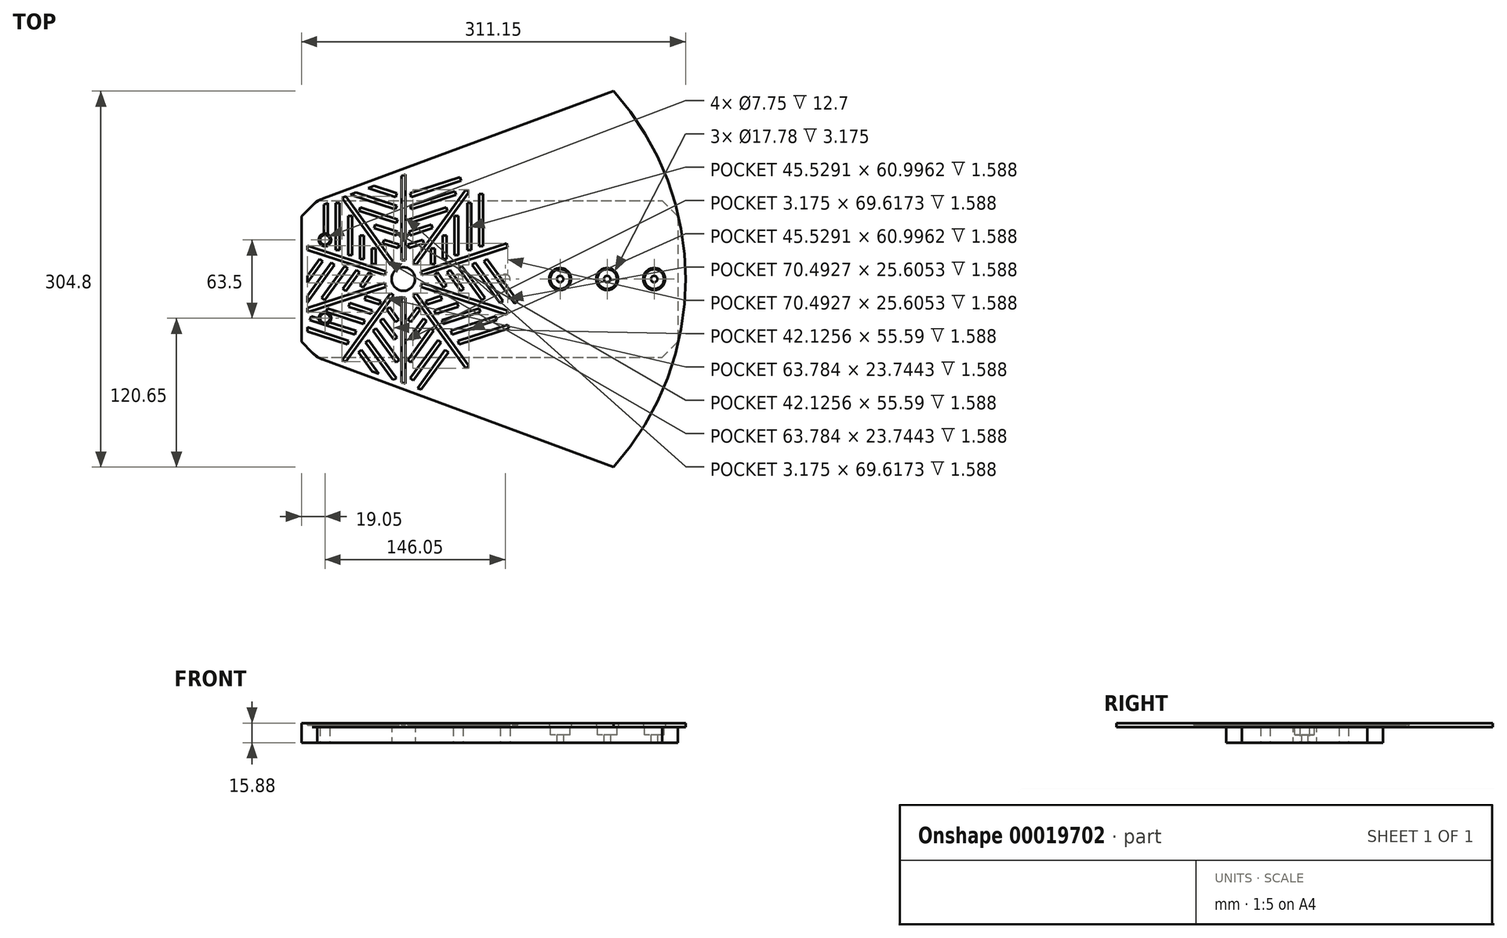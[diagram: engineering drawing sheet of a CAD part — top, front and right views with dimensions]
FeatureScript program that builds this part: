
annotation { "Feature Type Name" : "Feature", "Feature Type Description" : "" }
export const myFeature = defineFeature(function(context is Context, id is Id, definition is map)
    precondition{}
    {
        {
            var Q0;
            Q0=qCreatedBy(makeId("Top.planeOp"),FACE);
            var sketch = newSketch(context, id + "F0", { "sketchPlane" : qUnion([Q0])});
            skLineSegment(sketch, "E0.bottom", {"start": v(-127, 63.5) * mm, "end": v(177.8, 63.5) * mm});
            skLineSegment(sketch, "E0.top", {"start": v(-127, -63.5) * mm, "end": v(177.8, -63.5) * mm});
            skLineSegment(sketch, "E0.left", {"start": v(-127, 63.5) * mm, "end": v(-127, -63.5) * mm});
            skLineSegment(sketch, "E0.right", {"start": v(177.8, 63.5) * mm, "end": v(177.8, -63.5) * mm});
            skLineSegment(sketch, "E1", {"start": v(-127, 0) * mm, "end": v(177.8, 0) * mm, "construction": true});
            skSolve(sketch);
        }
        {
            var Q0;
            Q0 = qSketchRegion(id + "F0", true);
            extrude(context, id + "F1", {"entities" : qUnion([Q0]), "depth" : 12.7 * mm});
        }
        {
            var Q0;
            Q0=makeQuery(id+"F1.opExtrude","SWEPT_EDGE",EDGE,{"disambiguationData":[OSD([sQuery(id+"F0.wireOp",EDGE,"E0.top"),sQuery(id+"F0.wireOp",EDGE,"E0.left")])]});
            var Q1;
            Q1=makeQuery(id+"F1.opExtrude","SWEPT_EDGE",EDGE,{"disambiguationData":[OSD([sQuery(id+"F0.wireOp",EDGE,"E0.top"),sQuery(id+"F0.wireOp",EDGE,"E0.right")])]});
            var Q2;
            Q2=makeQuery(id+"F1.opExtrude","SWEPT_EDGE",EDGE,{"disambiguationData":[OSD([sQuery(id+"F0.wireOp",EDGE,"E0.bottom"),sQuery(id+"F0.wireOp",EDGE,"E0.right")])]});
            var Q3;
            Q3=makeQuery(id+"F1.opExtrude","SWEPT_EDGE",EDGE,{"disambiguationData":[OSD([sQuery(id+"F0.wireOp",EDGE,"E0.bottom"),sQuery(id+"F0.wireOp",EDGE,"E0.left")])]});
            chamfer(context, id + "F2", {"entities" : qUnion([Q0, Q1, Q2, Q3]), "width" : 12.7 * mm, "tangentPropagation" : true});
        }
        {
            var Q0;
            Q0=qCreatedBy(makeId("Top.planeOp"),FACE);
            var sketch = newSketch(context, id + "F3", { "sketchPlane" : qUnion([Q0])});
            skCircle(sketch, "E2", {"center": v(-44.45, 0) * mm, "radius": 9.53 * mm});
            skSolve(sketch);
        }
        {
            var Q0;
            Q0 = qSketchRegion(id + "F3", true);
            extrude(context, id + "F4", {"entities" : qUnion([Q0]), "operationType" : NewBodyOperationType.REMOVE, "depth" : 25.4 * mm});
        }
        {
            var Q0;
            Q0=qCreatedBy(makeId("Top.planeOp"),FACE);
            var sketch = newSketch(context, id + "F5", { "sketchPlane" : qUnion([Q0])});
            skCircle(sketch, "E3", {"center": v(0, 0) * mm, "radius": 3.87 * mm});
            skCircle(sketch, "E4", {"center": v(38.1, 0) * mm, "radius": 3.87 * mm});
            skSolve(sketch);
        }
        {
            var Q0;
            Q0 = qSketchRegion(id + "F5", true);
            extrude(context, id + "F6", {"entities" : qUnion([Q0]), "operationType" : NewBodyOperationType.REMOVE, "endBound" : BoundingType.THROUGH_ALL, "depth" : 25.4 * mm});
        }
        {
            var Q0;
            Q0=qCreatedBy(makeId("Top.planeOp"),FACE);
            var sketch = newSketch(context, id + "F7", { "sketchPlane" : qUnion([Q0])});
            skCircle(sketch, "E5", {"center": v(-107.95, 31.75) * mm, "radius": 3.87 * mm});
            skCircle(sketch, "E6", {"center": v(-107.95, -31.75) * mm, "radius": 3.87 * mm});
            skLineSegment(sketch, "E7", {"start": v(-107.95, 31.75) * mm, "end": v(-107.95, 0) * mm, "construction": true});
            skLineSegment(sketch, "E8", {"start": v(-107.95, 0) * mm, "end": v(-107.95, -31.75) * mm, "construction": true});
            skSolve(sketch);
        }
        {
            var Q0;
            Q0 = qSketchRegion(id + "F7", true);
            extrude(context, id + "F8", {"entities" : qUnion([Q0]), "operationType" : NewBodyOperationType.REMOVE, "endBound" : BoundingType.THROUGH_ALL, "depth" : 25.4 * mm});
        }
        {
            var Q0;
            Q0=qCreatedBy(makeId("Top.planeOp"),FACE);
            var sketch = newSketch(context, id + "F9", { "sketchPlane" : qUnion([Q0])});
            skCircle(sketch, "E9", {"center": v(82.55, 0) * mm, "radius": 2.6 * mm});
            skCircle(sketch, "E10", {"center": v(120.65, 0) * mm, "radius": 2.6 * mm});
            skCircle(sketch, "E11", {"center": v(158.75, 0) * mm, "radius": 2.6 * mm});
            skSolve(sketch);
        }
        {
            var Q0;
            Q0 = qSketchRegion(id + "F9", true);
            extrude(context, id + "F10", {"entities" : qUnion([Q0]), "operationType" : NewBodyOperationType.REMOVE, "endBound" : BoundingType.THROUGH_ALL, "depth" : 25.4 * mm});
        }
        {
            var Q0;
            Q0=makeQuery(id+"F1.opExtrude","CAP_FACE",FACE,{"disambiguationData":[OSD([sQuery(id+"F0.wireOp",EDGE,"E0.bottom"),sQuery(id+"F0.wireOp",EDGE,"E0.top"),sQuery(id+"F0.wireOp",EDGE,"E0.left"),sQuery(id+"F0.wireOp",EDGE,"E0.right")])],"isStart":false});
            var sketch = newSketch(context, id + "F11", { "sketchPlane" : qUnion([Q0])});
            skCircle(sketch, "E12", {"center": v(82.55, 0) * mm, "radius": 7.94 * mm});
            skCircle(sketch, "E13", {"center": v(120.65, 0) * mm, "radius": 7.94 * mm});
            skCircle(sketch, "E14", {"center": v(158.75, 0) * mm, "radius": 7.94 * mm});
            skSolve(sketch);
        }
        {
            var Q0;
            Q0 = qSketchRegion(id + "F11", true);
            extrude(context, id + "F12", {"entities" : qUnion([Q0]), "operationType" : NewBodyOperationType.REMOVE, "oppositeDirection" : true, "depth" : 6.35 * mm});
        }
        {
            var Q0;
            Q0=makeQuery(id+"F1.opExtrude","CAP_FACE",FACE,{"disambiguationData":[OSD([sQuery(id+"F0.wireOp",EDGE,"E0.bottom"),sQuery(id+"F0.wireOp",EDGE,"E0.top"),sQuery(id+"F0.wireOp",EDGE,"E0.left"),sQuery(id+"F0.wireOp",EDGE,"E0.right")])],"isStart":false});
            var sketch = newSketch(context, id + "F13", { "sketchPlane" : qUnion([Q0])});
            skLineSegment(sketch, "E15", {"start": v(-114.3, 63.5) * mm, "end": v(-127, 50.8) * mm});
            skLineSegment(sketch, "E16", {"start": v(-127, 50.8) * mm, "end": v(-127, -50.8) * mm});
            skLineSegment(sketch, "E17", {"start": v(-127, -50.8) * mm, "end": v(-114.3, -63.5) * mm});
            skCircle(sketch, "E18", {"center": v(-44.45, 0) * mm, "radius": 9.53 * mm});
            skCircle(sketch, "E19", {"center": v(-107.95, 31.75) * mm, "radius": 5.08 * mm});
            skCircle(sketch, "E20", {"center": v(-107.95, -31.75) * mm, "radius": 5.08 * mm});
            skCircle(sketch, "E21", {"center": v(82.55, 0) * mm, "radius": 8.9 * mm});
            skCircle(sketch, "E22", {"center": v(120.65, 0) * mm, "radius": 8.9 * mm});
            skCircle(sketch, "E23", {"center": v(158.75, 0) * mm, "radius": 8.9 * mm});
            skArc(sketch, "E24", {"start": v(125.94, -152.4) * mm, "mid": v(184.15, 0) * mm, "end": v(125.94, 152.4) * mm});
            skLineSegment(sketch, "E25", {"start": v(125.94, 152.4) * mm, "end": v(-114.3, 63.5) * mm});
            skLineSegment(sketch, "E26", {"start": v(125.94, -152.4) * mm, "end": v(-114.3, -63.5) * mm});
            skSolve(sketch);
        }
        {
            var Q0;
            Q0 = qSketchRegion(id + "F13", true);
            extrude(context, id + "F14", {"entities" : qUnion([Q0]), "depth" : 3.17 * mm});
        }
        {
            var Q0;
            Q0=makeQuery(id+"F14.opExtrude","SWEPT_EDGE",EDGE,{"disambiguationData":[OSD([sQuery(id+"F0.wireOp",EDGE,"E0.top"),sQuery(id+"F13.wireOp",EDGE,"57cfe194-b62b-4812-afb6-fe91522246ce"),sQuery(id+"F13.wireOp",EDGE,"734bb57e-c6ad-416e-8475-7722df8ed6a9.trimOffspring")])]});
            var Q1;
            Q1=makeQuery(id+"F14.opExtrude","SWEPT_EDGE",EDGE,{"disambiguationData":[OSD([sQuery(id+"F0.wireOp",EDGE,"E0.bottom"),sQuery(id+"F13.wireOp",EDGE,"7a98ed83-fb18-41a4-aa8c-db8b72770291"),sQuery(id+"F13.wireOp",EDGE,"12061aba-ef82-4446-8aa9-4ede10bfcb81")])]});
            fillet(context, id + "F15", {"entities" : qUnion([Q0, Q1]), "radius" : 25.4 * mm, "tangentPropagation" : true, "allowEdgeOverflow" : false});
        }
        {
            var Q0;
            Q0=makeQuery(id+"F14.opExtrude","CAP_FACE",FACE,{"disambiguationData":[OSD([sQuery(id+"F13.wireOp",EDGE,"E15"),sQuery(id+"F13.wireOp",EDGE,"E16"),sQuery(id+"F13.wireOp",EDGE,"E17"),sQuery(id+"F13.wireOp",EDGE,"E18"),sQuery(id+"F13.wireOp",EDGE,"E19"),sQuery(id+"F13.wireOp",EDGE,"E20"),sQuery(id+"F13.wireOp",EDGE,"E21"),sQuery(id+"F13.wireOp",EDGE,"E22"),sQuery(id+"F13.wireOp",EDGE,"E23"),sQuery(id+"F13.wireOp",EDGE,"E24"),sQuery(id+"F13.wireOp",EDGE,"E25"),sQuery(id+"F13.wireOp",EDGE,"E26")])],"isStart":false});
            var sketch = newSketch(context, id + "F16", { "sketchPlane" : qUnion([Q0])});
            skLineSegment(sketch, "E27.bottom", {"start": v(-46.04, 15.24) * mm, "end": v(-42.86, 15.24) * mm});
            skLineSegment(sketch, "E27.top", {"start": v(-46.04, 88.33) * mm, "end": v(-42.86, 88.33) * mm});
            skLineSegment(sketch, "E27.left", {"start": v(-46.04, 15.24) * mm, "end": v(-46.04, 88.33) * mm});
            skLineSegment(sketch, "E27.right", {"start": v(-42.86, 15.24) * mm, "end": v(-42.86, 88.33) * mm});
            skLineSegment(sketch, "E28.1.0", {"start": v(-54.7, 11.4) * mm, "end": v(-97.65, 70.53) * mm});
            skLineSegment(sketch, "E28.1.1", {"start": v(-52.12, 13.26) * mm, "end": v(-95.08, 72.4) * mm});
            skLineSegment(sketch, "E28.1.2", {"start": v(-97.65, 70.53) * mm, "end": v(-95.08, 72.4) * mm});
            skLineSegment(sketch, "E28.1.3", {"start": v(-54.7, 11.4) * mm, "end": v(-52.12, 13.26) * mm});
            skLineSegment(sketch, "E28.2.0", {"start": v(-59.43, 3.2) * mm, "end": v(-128.95, 25.79) * mm});
            skLineSegment(sketch, "E28.2.1", {"start": v(-58.45, 6.22) * mm, "end": v(-127.97, 28.8) * mm});
            skLineSegment(sketch, "E28.2.2", {"start": v(-128.95, 25.79) * mm, "end": v(-127.97, 28.8) * mm});
            skLineSegment(sketch, "E28.2.3", {"start": v(-59.43, 3.2) * mm, "end": v(-58.45, 6.22) * mm});
            skLineSegment(sketch, "E28.3.0", {"start": v(-58.45, -6.22) * mm, "end": v(-127.97, -28.8) * mm});
            skLineSegment(sketch, "E28.3.1", {"start": v(-59.43, -3.2) * mm, "end": v(-128.95, -25.79) * mm});
            skLineSegment(sketch, "E28.3.2", {"start": v(-127.97, -28.8) * mm, "end": v(-128.95, -25.79) * mm});
            skLineSegment(sketch, "E28.3.3", {"start": v(-58.45, -6.22) * mm, "end": v(-59.43, -3.2) * mm});
            skLineSegment(sketch, "E28.4.0", {"start": v(-52.12, -13.26) * mm, "end": v(-95.08, -72.4) * mm});
            skLineSegment(sketch, "E28.4.1", {"start": v(-54.7, -11.4) * mm, "end": v(-97.65, -70.53) * mm});
            skLineSegment(sketch, "E28.4.2", {"start": v(-95.08, -72.4) * mm, "end": v(-97.65, -70.53) * mm});
            skLineSegment(sketch, "E28.4.3", {"start": v(-52.12, -13.26) * mm, "end": v(-54.7, -11.4) * mm});
            skLineSegment(sketch, "E28.5.0", {"start": v(-42.86, -15.24) * mm, "end": v(-42.86, -88.33) * mm});
            skLineSegment(sketch, "E28.5.1", {"start": v(-46.04, -15.24) * mm, "end": v(-46.04, -88.33) * mm});
            skLineSegment(sketch, "E28.5.2", {"start": v(-42.86, -88.33) * mm, "end": v(-46.04, -88.33) * mm});
            skLineSegment(sketch, "E28.5.3", {"start": v(-42.86, -15.24) * mm, "end": v(-46.04, -15.24) * mm});
            skLineSegment(sketch, "E28.6.0", {"start": v(-34.2, -11.4) * mm, "end": v(8.75, -70.53) * mm});
            skLineSegment(sketch, "E28.6.1", {"start": v(-36.78, -13.26) * mm, "end": v(6.18, -72.4) * mm});
            skLineSegment(sketch, "E28.6.2", {"start": v(8.75, -70.53) * mm, "end": v(6.18, -72.4) * mm});
            skLineSegment(sketch, "E28.6.3", {"start": v(-34.2, -11.4) * mm, "end": v(-36.78, -13.26) * mm});
            skLineSegment(sketch, "E28.7.0", {"start": v(-29.47, -3.2) * mm, "end": v(40.05, -25.79) * mm});
            skLineSegment(sketch, "E28.7.1", {"start": v(-30.45, -6.22) * mm, "end": v(39.07, -28.8) * mm});
            skLineSegment(sketch, "E28.7.2", {"start": v(40.05, -25.79) * mm, "end": v(39.07, -28.8) * mm});
            skLineSegment(sketch, "E28.7.3", {"start": v(-29.47, -3.2) * mm, "end": v(-30.45, -6.22) * mm});
            skLineSegment(sketch, "E28.8.0", {"start": v(-30.45, 6.22) * mm, "end": v(39.07, 28.8) * mm});
            skLineSegment(sketch, "E28.8.1", {"start": v(-29.47, 3.2) * mm, "end": v(40.05, 25.79) * mm});
            skLineSegment(sketch, "E28.8.2", {"start": v(39.07, 28.8) * mm, "end": v(40.05, 25.79) * mm});
            skLineSegment(sketch, "E28.8.3", {"start": v(-30.45, 6.22) * mm, "end": v(-29.47, 3.2) * mm});
            skLineSegment(sketch, "E28.9.0", {"start": v(-36.78, 13.26) * mm, "end": v(6.18, 72.4) * mm});
            skLineSegment(sketch, "E28.9.1", {"start": v(-34.2, 11.4) * mm, "end": v(8.75, 70.53) * mm});
            skLineSegment(sketch, "E28.9.2", {"start": v(6.18, 72.4) * mm, "end": v(8.75, 70.53) * mm});
            skLineSegment(sketch, "E28.9.3", {"start": v(-36.78, 13.26) * mm, "end": v(-34.2, 11.4) * mm});
            skPoint(sketch, "E28.center", {"position": v(-44.45, 0) * mm});
            skLineSegment(sketch, "E29.bottom", {"start": v(0.17, 51.12) * mm, "end": v(-3, 51.12) * mm});
            skLineSegment(sketch, "E29.top", {"start": v(0.17, 19.37) * mm, "end": v(-3, 19.37) * mm});
            skLineSegment(sketch, "E29.left", {"start": v(0.17, 51.12) * mm, "end": v(0.17, 19.37) * mm});
            skLineSegment(sketch, "E29.right", {"start": v(-3, 51.12) * mm, "end": v(-3, 19.37) * mm});
            skLineSegment(sketch, "E30.bottom", {"start": v(-12.53, 35.33) * mm, "end": v(-9.35, 35.33) * mm});
            skLineSegment(sketch, "E30.top", {"start": v(-12.53, 16.28) * mm, "end": v(-9.35, 16.28) * mm});
            skLineSegment(sketch, "E30.left", {"start": v(-12.53, 35.33) * mm, "end": v(-12.53, 16.28) * mm});
            skLineSegment(sketch, "E30.right", {"start": v(-9.35, 35.33) * mm, "end": v(-9.35, 16.28) * mm});
            skLineSegment(sketch, "E31.bottom", {"start": v(7.3, 61.65) * mm, "end": v(10.48, 61.65) * mm});
            skLineSegment(sketch, "E31.top", {"start": v(7.3, 23.55) * mm, "end": v(10.48, 23.55) * mm});
            skLineSegment(sketch, "E31.left", {"start": v(7.3, 61.65) * mm, "end": v(7.3, 23.55) * mm});
            skLineSegment(sketch, "E31.right", {"start": v(10.48, 61.65) * mm, "end": v(10.48, 23.55) * mm});
            skLineSegment(sketch, "E32.bottom", {"start": v(-22.05, 24.68) * mm, "end": v(-18.88, 24.68) * mm});
            skLineSegment(sketch, "E32.top", {"start": v(-22.05, 11.98) * mm, "end": v(-18.88, 11.98) * mm});
            skLineSegment(sketch, "E32.left", {"start": v(-22.05, 24.68) * mm, "end": v(-22.05, 11.98) * mm});
            skLineSegment(sketch, "E32.right", {"start": v(-18.88, 24.68) * mm, "end": v(-18.88, 11.98) * mm});
            skLineSegment(sketch, "E33.bottom", {"start": v(16.83, 26.62) * mm, "end": v(20, 26.62) * mm});
            skLineSegment(sketch, "E33.top", {"start": v(16.83, 68.97) * mm, "end": v(20, 68.97) * mm});
            skLineSegment(sketch, "E33.left", {"start": v(16.83, 26.62) * mm, "end": v(16.83, 68.97) * mm});
            skLineSegment(sketch, "E33.right", {"start": v(20, 26.62) * mm, "end": v(20, 68.97) * mm});
            skLineSegment(sketch, "E34", {"start": v(-29.96, 4.7) * mm, "end": v(39.56, 27.3) * mm, "construction": true});
            skLineSegment(sketch, "E35.MirrorCS", {"start": v(23.34, 16.35) * mm, "end": v(48.24, -17.91) * mm});
            skLineSegment(sketch, "E36.MirrorCS", {"start": v(20.77, 14.49) * mm, "end": v(45.67, -19.78) * mm});
            skLineSegment(sketch, "E37.MirrorCS", {"start": v(45.67, -19.78) * mm, "end": v(48.24, -17.91) * mm});
            skLineSegment(sketch, "E38.MirrorCS", {"start": v(20.77, 14.49) * mm, "end": v(23.34, 16.35) * mm});
            skLineSegment(sketch, "E39.MirrorCS", {"start": v(36.23, -17.59) * mm, "end": v(13.83, 13.24) * mm});
            skLineSegment(sketch, "E40.MirrorCS", {"start": v(33.66, -19.45) * mm, "end": v(11.26, 11.37) * mm});
            skLineSegment(sketch, "E41.MirrorCS", {"start": v(33.66, -19.45) * mm, "end": v(36.23, -17.59) * mm});
            skLineSegment(sketch, "E42.MirrorCS", {"start": v(11.26, 11.37) * mm, "end": v(13.83, 13.24) * mm});
            skLineSegment(sketch, "E43.MirrorCS", {"start": v(21.7, -15.13) * mm, "end": v(19.13, -17) * mm});
            skLineSegment(sketch, "E44.MirrorCS", {"start": v(21.7, -15.13) * mm, "end": v(3.04, 10.56) * mm});
            skLineSegment(sketch, "E45.MirrorCS", {"start": v(19.13, -17) * mm, "end": v(0.47, 8.69) * mm});
            skLineSegment(sketch, "E46.MirrorCS", {"start": v(3.04, 10.56) * mm, "end": v(0.47, 8.69) * mm});
            skLineSegment(sketch, "E47.MirrorCS", {"start": v(4.7, -7.95) * mm, "end": v(-6.49, 7.46) * mm});
            skLineSegment(sketch, "E48.MirrorCS", {"start": v(2.14, -9.82) * mm, "end": v(-9.06, 5.6) * mm});
            skLineSegment(sketch, "E49.MirrorCS", {"start": v(2.14, -9.82) * mm, "end": v(4.7, -7.95) * mm});
            skLineSegment(sketch, "E50.MirrorCS", {"start": v(-9.06, 5.6) * mm, "end": v(-6.49, 7.46) * mm});
            skLineSegment(sketch, "E51.MirrorCS", {"start": v(-11.82, -6.8) * mm, "end": v(-9.25, -4.94) * mm});
            skLineSegment(sketch, "E52.MirrorCS", {"start": v(-9.25, -4.94) * mm, "end": v(-16.72, 5.34) * mm});
            skLineSegment(sketch, "E53.MirrorCS", {"start": v(-19.29, 3.47) * mm, "end": v(-16.72, 5.34) * mm});
            skLineSegment(sketch, "E54.MirrorCS", {"start": v(-11.82, -6.8) * mm, "end": v(-19.29, 3.47) * mm});
            skLineSegment(sketch, "E55.1.0", {"start": v(-49.85, 69.53) * mm, "end": v(-90.13, 82.62) * mm});
            skLineSegment(sketch, "E55.1.1", {"start": v(-91.1, 79.6) * mm, "end": v(-90.13, 82.62) * mm});
            skLineSegment(sketch, "E55.1.2", {"start": v(-50.83, 66.5) * mm, "end": v(-49.85, 69.53) * mm});
            skLineSegment(sketch, "E55.1.3", {"start": v(-50.83, 66.5) * mm, "end": v(-91.1, 79.6) * mm});
            skLineSegment(sketch, "E55.1.4", {"start": v(-86.1, 71.3) * mm, "end": v(-49.87, 59.52) * mm});
            skLineSegment(sketch, "E55.1.5", {"start": v(-87.09, 68.27) * mm, "end": v(-50.85, 56.5) * mm});
            skLineSegment(sketch, "E55.1.6", {"start": v(-50.85, 56.5) * mm, "end": v(-49.87, 59.52) * mm});
            skLineSegment(sketch, "E55.1.7", {"start": v(-87.09, 68.27) * mm, "end": v(-86.1, 71.3) * mm});
            skLineSegment(sketch, "E55.1.8", {"start": v(-79.28, 58.24) * mm, "end": v(-80.26, 55.22) * mm});
            skLineSegment(sketch, "E55.1.9", {"start": v(-79.28, 58.24) * mm, "end": v(-49.09, 48.42) * mm});
            skLineSegment(sketch, "E55.1.10", {"start": v(-80.26, 55.22) * mm, "end": v(-50.07, 45.4) * mm});
            skLineSegment(sketch, "E55.1.11", {"start": v(-49.09, 48.42) * mm, "end": v(-50.07, 45.4) * mm});
            skLineSegment(sketch, "E55.1.12", {"start": v(-67.2, 44.3) * mm, "end": v(-49.09, 38.4) * mm});
            skLineSegment(sketch, "E55.1.13", {"start": v(-68.18, 41.28) * mm, "end": v(-50.07, 35.39) * mm});
            skLineSegment(sketch, "E55.1.14", {"start": v(-68.18, 41.28) * mm, "end": v(-67.2, 44.3) * mm});
            skLineSegment(sketch, "E55.1.15", {"start": v(-50.07, 35.39) * mm, "end": v(-49.09, 38.4) * mm});
            skLineSegment(sketch, "E55.1.16", {"start": v(-60.02, 31.95) * mm, "end": v(-47.94, 28.02) * mm});
            skLineSegment(sketch, "E55.1.17", {"start": v(-61, 28.93) * mm, "end": v(-60.02, 31.95) * mm});
            skLineSegment(sketch, "E55.1.18", {"start": v(-61, 28.93) * mm, "end": v(-48.92, 25) * mm});
            skLineSegment(sketch, "E55.1.19", {"start": v(-48.92, 25) * mm, "end": v(-47.94, 28.02) * mm});
            skLineSegment(sketch, "E55.1.20", {"start": v(-39.98, 25) * mm, "end": v(-40.96, 28.02) * mm});
            skLineSegment(sketch, "E55.1.21", {"start": v(-28.88, 31.95) * mm, "end": v(-40.96, 28.02) * mm});
            skLineSegment(sketch, "E55.1.22", {"start": v(-27.9, 28.93) * mm, "end": v(-39.98, 25) * mm});
            skLineSegment(sketch, "E55.1.23", {"start": v(-27.9, 28.93) * mm, "end": v(-28.88, 31.95) * mm});
            skLineSegment(sketch, "E55.1.24", {"start": v(-38.83, 35.39) * mm, "end": v(-39.81, 38.4) * mm});
            skLineSegment(sketch, "E55.1.25", {"start": v(-21.7, 44.3) * mm, "end": v(-39.81, 38.4) * mm});
            skLineSegment(sketch, "E55.1.26", {"start": v(-20.72, 41.28) * mm, "end": v(-38.83, 35.39) * mm});
            skLineSegment(sketch, "E55.1.27", {"start": v(-20.72, 41.28) * mm, "end": v(-21.7, 44.3) * mm});
            skLineSegment(sketch, "E55.1.28", {"start": v(-8.64, 55.22) * mm, "end": v(-38.83, 45.4) * mm});
            skLineSegment(sketch, "E55.1.29", {"start": v(-9.62, 58.24) * mm, "end": v(-39.81, 48.42) * mm});
            skLineSegment(sketch, "E55.1.30", {"start": v(-9.62, 58.24) * mm, "end": v(-8.64, 55.22) * mm});
            skLineSegment(sketch, "E55.1.31", {"start": v(-39.81, 48.42) * mm, "end": v(-38.83, 45.4) * mm});
            skLineSegment(sketch, "E55.1.32", {"start": v(-2.8, 71.3) * mm, "end": v(-39.03, 59.52) * mm});
            skLineSegment(sketch, "E55.1.33", {"start": v(-1.81, 68.27) * mm, "end": v(-38.05, 56.5) * mm});
            skLineSegment(sketch, "E55.1.34", {"start": v(-38.05, 56.5) * mm, "end": v(-39.03, 59.52) * mm});
            skLineSegment(sketch, "E55.1.35", {"start": v(-1.81, 68.27) * mm, "end": v(-2.8, 71.3) * mm});
            skLineSegment(sketch, "E55.1.36", {"start": v(-38.07, 66.5) * mm, "end": v(2.2, 79.6) * mm});
            skLineSegment(sketch, "E55.1.37", {"start": v(-39.05, 69.53) * mm, "end": v(1.23, 82.62) * mm});
            skLineSegment(sketch, "E55.1.38", {"start": v(2.2, 79.6) * mm, "end": v(1.23, 82.62) * mm});
            skLineSegment(sketch, "E55.1.39", {"start": v(-38.07, 66.5) * mm, "end": v(-39.05, 69.53) * mm});
            skLineSegment(sketch, "E55.2.0", {"start": v(-112.24, 16.35) * mm, "end": v(-137.14, -17.91) * mm});
            skLineSegment(sketch, "E55.2.1", {"start": v(-134.57, -19.78) * mm, "end": v(-137.14, -17.91) * mm});
            skLineSegment(sketch, "E55.2.2", {"start": v(-109.67, 14.49) * mm, "end": v(-112.24, 16.35) * mm});
            skLineSegment(sketch, "E55.2.3", {"start": v(-109.67, 14.49) * mm, "end": v(-134.57, -19.78) * mm});
            skLineSegment(sketch, "E55.2.4", {"start": v(-125.13, -17.59) * mm, "end": v(-102.73, 13.24) * mm});
            skLineSegment(sketch, "E55.2.5", {"start": v(-122.56, -19.45) * mm, "end": v(-100.16, 11.37) * mm});
            skLineSegment(sketch, "E55.2.6", {"start": v(-100.16, 11.37) * mm, "end": v(-102.73, 13.24) * mm});
            skLineSegment(sketch, "E55.2.7", {"start": v(-122.56, -19.45) * mm, "end": v(-125.13, -17.59) * mm});
            skLineSegment(sketch, "E55.2.8", {"start": v(-110.6, -15.13) * mm, "end": v(-108.03, -17) * mm});
            skLineSegment(sketch, "E55.2.9", {"start": v(-110.6, -15.13) * mm, "end": v(-91.94, 10.56) * mm});
            skLineSegment(sketch, "E55.2.10", {"start": v(-108.03, -17) * mm, "end": v(-89.37, 8.69) * mm});
            skLineSegment(sketch, "E55.2.11", {"start": v(-91.94, 10.56) * mm, "end": v(-89.37, 8.69) * mm});
            skLineSegment(sketch, "E55.2.12", {"start": v(-93.6, -7.95) * mm, "end": v(-82.41, 7.46) * mm});
            skLineSegment(sketch, "E55.2.13", {"start": v(-91.04, -9.82) * mm, "end": v(-79.84, 5.6) * mm});
            skLineSegment(sketch, "E55.2.14", {"start": v(-91.04, -9.82) * mm, "end": v(-93.6, -7.95) * mm});
            skLineSegment(sketch, "E55.2.15", {"start": v(-79.84, 5.6) * mm, "end": v(-82.41, 7.46) * mm});
            skLineSegment(sketch, "E55.2.16", {"start": v(-79.65, -4.94) * mm, "end": v(-72.18, 5.34) * mm});
            skLineSegment(sketch, "E55.2.17", {"start": v(-77.08, -6.8) * mm, "end": v(-79.65, -4.94) * mm});
            skLineSegment(sketch, "E55.2.18", {"start": v(-77.08, -6.8) * mm, "end": v(-69.61, 3.47) * mm});
            skLineSegment(sketch, "E55.2.19", {"start": v(-69.61, 3.47) * mm, "end": v(-72.18, 5.34) * mm});
            skLineSegment(sketch, "E55.2.20", {"start": v(-66.85, 11.98) * mm, "end": v(-70.02, 11.98) * mm});
            skLineSegment(sketch, "E55.2.21", {"start": v(-70.02, 24.68) * mm, "end": v(-70.02, 11.98) * mm});
            skLineSegment(sketch, "E55.2.22", {"start": v(-66.85, 24.68) * mm, "end": v(-66.85, 11.98) * mm});
            skLineSegment(sketch, "E55.2.23", {"start": v(-66.85, 24.68) * mm, "end": v(-70.02, 24.68) * mm});
            skLineSegment(sketch, "E55.2.24", {"start": v(-76.37, 16.28) * mm, "end": v(-79.55, 16.28) * mm});
            skLineSegment(sketch, "E55.2.25", {"start": v(-79.55, 35.33) * mm, "end": v(-79.55, 16.28) * mm});
            skLineSegment(sketch, "E55.2.26", {"start": v(-76.37, 35.33) * mm, "end": v(-76.37, 16.28) * mm});
            skLineSegment(sketch, "E55.2.27", {"start": v(-76.37, 35.33) * mm, "end": v(-79.55, 35.33) * mm});
            skLineSegment(sketch, "E55.2.28", {"start": v(-85.9, 51.12) * mm, "end": v(-85.9, 19.37) * mm});
            skLineSegment(sketch, "E55.2.29", {"start": v(-89.07, 51.12) * mm, "end": v(-89.07, 19.37) * mm});
            skLineSegment(sketch, "E55.2.30", {"start": v(-89.07, 51.12) * mm, "end": v(-85.9, 51.12) * mm});
            skLineSegment(sketch, "E55.2.31", {"start": v(-89.07, 19.37) * mm, "end": v(-85.9, 19.37) * mm});
            skLineSegment(sketch, "E55.2.32", {"start": v(-99.38, 61.65) * mm, "end": v(-99.38, 23.55) * mm});
            skLineSegment(sketch, "E55.2.33", {"start": v(-96.2, 61.65) * mm, "end": v(-96.2, 23.55) * mm});
            skLineSegment(sketch, "E55.2.34", {"start": v(-96.2, 23.55) * mm, "end": v(-99.38, 23.55) * mm});
            skLineSegment(sketch, "E55.2.35", {"start": v(-96.2, 61.65) * mm, "end": v(-99.38, 61.65) * mm});
            skLineSegment(sketch, "E55.2.36", {"start": v(-105.73, 26.62) * mm, "end": v(-105.73, 68.97) * mm});
            skLineSegment(sketch, "E55.2.37", {"start": v(-108.9, 26.62) * mm, "end": v(-108.9, 68.97) * mm});
            skLineSegment(sketch, "E55.2.38", {"start": v(-105.73, 68.97) * mm, "end": v(-108.9, 68.97) * mm});
            skLineSegment(sketch, "E55.2.39", {"start": v(-105.73, 26.62) * mm, "end": v(-108.9, 26.62) * mm});
            skLineSegment(sketch, "E55.3.0", {"start": v(-80.95, -59.42) * mm, "end": v(-56.06, -93.69) * mm});
            skLineSegment(sketch, "E55.3.1", {"start": v(-53.49, -91.82) * mm, "end": v(-56.06, -93.69) * mm});
            skLineSegment(sketch, "E55.3.2", {"start": v(-78.38, -57.56) * mm, "end": v(-80.95, -59.42) * mm});
            skLineSegment(sketch, "E55.3.3", {"start": v(-78.38, -57.56) * mm, "end": v(-53.49, -91.82) * mm});
            skLineSegment(sketch, "E55.3.4", {"start": v(-52.65, -82.16) * mm, "end": v(-75.05, -51.34) * mm});
            skLineSegment(sketch, "E55.3.5", {"start": v(-50.09, -80.3) * mm, "end": v(-72.48, -49.47) * mm});
            skLineSegment(sketch, "E55.3.6", {"start": v(-72.48, -49.47) * mm, "end": v(-75.05, -51.34) * mm});
            skLineSegment(sketch, "E55.3.7", {"start": v(-50.09, -80.3) * mm, "end": v(-52.65, -82.16) * mm});
            skLineSegment(sketch, "E55.3.8", {"start": v(-50.5, -67.59) * mm, "end": v(-47.93, -65.72) * mm});
            skLineSegment(sketch, "E55.3.9", {"start": v(-50.5, -67.59) * mm, "end": v(-69.16, -41.9) * mm});
            skLineSegment(sketch, "E55.3.10", {"start": v(-47.93, -65.72) * mm, "end": v(-66.6, -40.03) * mm});
            skLineSegment(sketch, "E55.3.11", {"start": v(-69.16, -41.9) * mm, "end": v(-66.6, -40.03) * mm});
            skLineSegment(sketch, "E55.3.12", {"start": v(-52.08, -49.21) * mm, "end": v(-63.28, -33.8) * mm});
            skLineSegment(sketch, "E55.3.13", {"start": v(-49.51, -47.34) * mm, "end": v(-60.7, -31.93) * mm});
            skLineSegment(sketch, "E55.3.14", {"start": v(-49.51, -47.34) * mm, "end": v(-52.08, -49.21) * mm});
            skLineSegment(sketch, "E55.3.15", {"start": v(-60.7, -31.93) * mm, "end": v(-63.28, -33.8) * mm});
            skLineSegment(sketch, "E55.3.16", {"start": v(-50.63, -35) * mm, "end": v(-58.1, -24.72) * mm});
            skLineSegment(sketch, "E55.3.17", {"start": v(-48.06, -33.13) * mm, "end": v(-50.63, -35) * mm});
            skLineSegment(sketch, "E55.3.18", {"start": v(-48.06, -33.13) * mm, "end": v(-55.53, -22.86) * mm});
            skLineSegment(sketch, "E55.3.19", {"start": v(-55.53, -22.86) * mm, "end": v(-58.1, -24.72) * mm});
            skLineSegment(sketch, "E55.3.20", {"start": v(-62.77, -17.6) * mm, "end": v(-63.75, -20.62) * mm});
            skLineSegment(sketch, "E55.3.21", {"start": v(-75.83, -16.7) * mm, "end": v(-63.75, -20.62) * mm});
            skLineSegment(sketch, "E55.3.22", {"start": v(-74.84, -13.67) * mm, "end": v(-62.77, -17.6) * mm});
            skLineSegment(sketch, "E55.3.23", {"start": v(-74.84, -13.67) * mm, "end": v(-75.83, -16.7) * mm});
            skLineSegment(sketch, "E55.3.24", {"start": v(-69.8, -25.33) * mm, "end": v(-70.78, -28.35) * mm});
            skLineSegment(sketch, "E55.3.25", {"start": v(-88.9, -22.46) * mm, "end": v(-70.78, -28.35) * mm});
            skLineSegment(sketch, "E55.3.26", {"start": v(-87.91, -19.44) * mm, "end": v(-69.8, -25.33) * mm});
            skLineSegment(sketch, "E55.3.27", {"start": v(-87.91, -19.44) * mm, "end": v(-88.9, -22.46) * mm});
            skLineSegment(sketch, "E55.3.28", {"start": v(-105.88, -23.62) * mm, "end": v(-75.68, -33.43) * mm});
            skLineSegment(sketch, "E55.3.29", {"start": v(-106.86, -26.64) * mm, "end": v(-76.66, -36.45) * mm});
            skLineSegment(sketch, "E55.3.30", {"start": v(-106.86, -26.64) * mm, "end": v(-105.88, -23.62) * mm});
            skLineSegment(sketch, "E55.3.31", {"start": v(-76.66, -36.45) * mm, "end": v(-75.68, -33.43) * mm});
            skLineSegment(sketch, "E55.3.32", {"start": v(-120.06, -33.2) * mm, "end": v(-83.82, -44.97) * mm});
            skLineSegment(sketch, "E55.3.33", {"start": v(-119.08, -30.17) * mm, "end": v(-82.84, -41.95) * mm});
            skLineSegment(sketch, "E55.3.34", {"start": v(-82.84, -41.95) * mm, "end": v(-83.82, -44.97) * mm});
            skLineSegment(sketch, "E55.3.35", {"start": v(-119.08, -30.17) * mm, "end": v(-120.06, -33.2) * mm});
            skLineSegment(sketch, "E55.3.36", {"start": v(-88.7, -50.06) * mm, "end": v(-128.98, -36.97) * mm});
            skLineSegment(sketch, "E55.3.37", {"start": v(-89.68, -53.08) * mm, "end": v(-129.97, -39.99) * mm});
            skLineSegment(sketch, "E55.3.38", {"start": v(-128.98, -36.97) * mm, "end": v(-129.97, -39.99) * mm});
            skLineSegment(sketch, "E55.3.39", {"start": v(-88.7, -50.06) * mm, "end": v(-89.68, -53.08) * mm});
            skLineSegment(sketch, "E55.4.0", {"start": v(0.78, -53.08) * mm, "end": v(41.07, -39.99) * mm});
            skLineSegment(sketch, "E55.4.1", {"start": v(40.08, -36.97) * mm, "end": v(41.07, -39.99) * mm});
            skLineSegment(sketch, "E55.4.2", {"start": v(-0.2, -50.06) * mm, "end": v(0.78, -53.08) * mm});
            skLineSegment(sketch, "E55.4.3", {"start": v(-0.2, -50.06) * mm, "end": v(40.08, -36.97) * mm});
            skLineSegment(sketch, "E55.4.4", {"start": v(31.16, -33.2) * mm, "end": v(-5.08, -44.97) * mm});
            skLineSegment(sketch, "E55.4.5", {"start": v(30.18, -30.17) * mm, "end": v(-6.06, -41.95) * mm});
            skLineSegment(sketch, "E55.4.6", {"start": v(-6.06, -41.95) * mm, "end": v(-5.08, -44.97) * mm});
            skLineSegment(sketch, "E55.4.7", {"start": v(30.18, -30.17) * mm, "end": v(31.16, -33.2) * mm});
            skLineSegment(sketch, "E55.4.8", {"start": v(17.96, -26.64) * mm, "end": v(16.98, -23.62) * mm});
            skLineSegment(sketch, "E55.4.9", {"start": v(17.96, -26.64) * mm, "end": v(-12.24, -36.45) * mm});
            skLineSegment(sketch, "E55.4.10", {"start": v(16.98, -23.62) * mm, "end": v(-13.22, -33.43) * mm});
            skLineSegment(sketch, "E55.4.11", {"start": v(-12.24, -36.45) * mm, "end": v(-13.22, -33.43) * mm});
            skLineSegment(sketch, "E55.4.12", {"start": v(0, -22.46) * mm, "end": v(-18.12, -28.35) * mm});
            skLineSegment(sketch, "E55.4.13", {"start": v(-0.99, -19.44) * mm, "end": v(-19.1, -25.33) * mm});
            skLineSegment(sketch, "E55.4.14", {"start": v(-0.99, -19.44) * mm, "end": v(0, -22.46) * mm});
            skLineSegment(sketch, "E55.4.15", {"start": v(-19.1, -25.33) * mm, "end": v(-18.12, -28.35) * mm});
            skLineSegment(sketch, "E55.4.16", {"start": v(-13.07, -16.7) * mm, "end": v(-25.15, -20.62) * mm});
            skLineSegment(sketch, "E55.4.17", {"start": v(-14.06, -13.67) * mm, "end": v(-13.07, -16.7) * mm});
            skLineSegment(sketch, "E55.4.18", {"start": v(-14.06, -13.67) * mm, "end": v(-26.13, -17.6) * mm});
            skLineSegment(sketch, "E55.4.19", {"start": v(-26.13, -17.6) * mm, "end": v(-25.15, -20.62) * mm});
            skLineSegment(sketch, "E55.4.20", {"start": v(-33.37, -22.86) * mm, "end": v(-30.8, -24.72) * mm});
            skLineSegment(sketch, "E55.4.21", {"start": v(-38.27, -35) * mm, "end": v(-30.8, -24.72) * mm});
            skLineSegment(sketch, "E55.4.22", {"start": v(-40.84, -33.13) * mm, "end": v(-33.37, -22.86) * mm});
            skLineSegment(sketch, "E55.4.23", {"start": v(-40.84, -33.13) * mm, "end": v(-38.27, -35) * mm});
            skLineSegment(sketch, "E55.4.24", {"start": v(-28.2, -31.93) * mm, "end": v(-25.62, -33.8) * mm});
            skLineSegment(sketch, "E55.4.25", {"start": v(-36.82, -49.21) * mm, "end": v(-25.62, -33.8) * mm});
            skLineSegment(sketch, "E55.4.26", {"start": v(-39.39, -47.34) * mm, "end": v(-28.2, -31.93) * mm});
            skLineSegment(sketch, "E55.4.27", {"start": v(-39.39, -47.34) * mm, "end": v(-36.82, -49.21) * mm});
            skLineSegment(sketch, "E55.4.28", {"start": v(-40.97, -65.72) * mm, "end": v(-22.3, -40.03) * mm});
            skLineSegment(sketch, "E55.4.29", {"start": v(-38.4, -67.59) * mm, "end": v(-19.74, -41.9) * mm});
            skLineSegment(sketch, "E55.4.30", {"start": v(-38.4, -67.59) * mm, "end": v(-40.97, -65.72) * mm});
            skLineSegment(sketch, "E55.4.31", {"start": v(-19.74, -41.9) * mm, "end": v(-22.3, -40.03) * mm});
            skLineSegment(sketch, "E55.4.32", {"start": v(-36.25, -82.16) * mm, "end": v(-13.85, -51.34) * mm});
            skLineSegment(sketch, "E55.4.33", {"start": v(-38.81, -80.3) * mm, "end": v(-16.42, -49.47) * mm});
            skLineSegment(sketch, "E55.4.34", {"start": v(-16.42, -49.47) * mm, "end": v(-13.85, -51.34) * mm});
            skLineSegment(sketch, "E55.4.35", {"start": v(-38.81, -80.3) * mm, "end": v(-36.25, -82.16) * mm});
            skLineSegment(sketch, "E55.4.36", {"start": v(-10.52, -57.56) * mm, "end": v(-35.41, -91.82) * mm});
            skLineSegment(sketch, "E55.4.37", {"start": v(-7.95, -59.42) * mm, "end": v(-32.84, -93.69) * mm});
            skLineSegment(sketch, "E55.4.38", {"start": v(-35.41, -91.82) * mm, "end": v(-32.84, -93.69) * mm});
            skLineSegment(sketch, "E55.4.39", {"start": v(-10.52, -57.56) * mm, "end": v(-7.95, -59.42) * mm});
            skSolve(sketch);
        }
        {
            var Q0;
            Q0 = qSketchRegion(id + "F16", true);
            extrude(context, id + "F17", {"entities" : qUnion([Q0]), "operationType" : NewBodyOperationType.REMOVE, "oppositeDirection" : true, "depth" : 1.59 * mm});
        }
        {
            var Q0;
            Q0=makeQuery(id+"F14.opExtrude","CAP_FACE",FACE,{"disambiguationData":[OSD([sQuery(id+"F13.wireOp",EDGE,"E15"),sQuery(id+"F13.wireOp",EDGE,"E16"),sQuery(id+"F13.wireOp",EDGE,"E17"),sQuery(id+"F13.wireOp",EDGE,"E18"),sQuery(id+"F13.wireOp",EDGE,"E19"),sQuery(id+"F13.wireOp",EDGE,"E20"),sQuery(id+"F13.wireOp",EDGE,"E21"),sQuery(id+"F13.wireOp",EDGE,"E22"),sQuery(id+"F13.wireOp",EDGE,"E23"),sQuery(id+"F13.wireOp",EDGE,"E24"),sQuery(id+"F13.wireOp",EDGE,"E25"),sQuery(id+"F13.wireOp",EDGE,"E26")])],"isStart":false});
            var sketch = newSketch(context, id + "F18", { "sketchPlane" : qUnion([Q0])});
            skLineSegment(sketch, "E56.0", {"start": v(125.94, -147.32) * mm, "end": v(-111.67, -59.4) * mm});
            skLineSegment(sketch, "E56.1", {"start": v(-122.24, -48.83) * mm, "end": v(-111.67, -59.4) * mm});
            skLineSegment(sketch, "E56.2", {"start": v(-122.24, 48.83) * mm, "end": v(-122.24, -48.83) * mm});
            skLineSegment(sketch, "E56.3", {"start": v(-111.67, 59.4) * mm, "end": v(-122.24, 48.83) * mm});
            skLineSegment(sketch, "E56.4", {"start": v(127.6, 147.93) * mm, "end": v(-111.67, 59.4) * mm});
            skLineSegment(sketch, "E57", {"start": v(125.94, -147.32) * mm, "end": v(125.94, -152.4) * mm});
            skLineSegment(sketch, "E58", {"start": v(125.94, -152.4) * mm, "end": v(-114.3, -63.5) * mm});
            skLineSegment(sketch, "E59", {"start": v(-114.3, -63.5) * mm, "end": v(-127, -50.8) * mm});
            skLineSegment(sketch, "E60", {"start": v(-127, -50.8) * mm, "end": v(-127, 50.8) * mm});
            skLineSegment(sketch, "E61", {"start": v(-127, 50.8) * mm, "end": v(-114.3, 63.5) * mm});
            skLineSegment(sketch, "E62", {"start": v(-114.3, 63.5) * mm, "end": v(125.94, 152.4) * mm});
            skLineSegment(sketch, "E63", {"start": v(125.94, 152.4) * mm, "end": v(127.6, 147.93) * mm});
            skSolve(sketch);
        }
        {
            var Q0;
            Q0 = qSketchRegion(id + "F18", true);
            var Q1;
            Q1=makeQuery(id+"F14.opExtrude","CAP_FACE",FACE,{"disambiguationData":[OSD([sQuery(id+"F13.wireOp",EDGE,"E15"),sQuery(id+"F13.wireOp",EDGE,"E16"),sQuery(id+"F13.wireOp",EDGE,"E17"),sQuery(id+"F13.wireOp",EDGE,"E18"),sQuery(id+"F13.wireOp",EDGE,"E19"),sQuery(id+"F13.wireOp",EDGE,"E20"),sQuery(id+"F13.wireOp",EDGE,"E21"),sQuery(id+"F13.wireOp",EDGE,"E22"),sQuery(id+"F13.wireOp",EDGE,"E23"),sQuery(id+"F13.wireOp",EDGE,"E24"),sQuery(id+"F13.wireOp",EDGE,"E25"),sQuery(id+"F13.wireOp",EDGE,"E26")])],"isStart":true});
            extrude(context, id + "F19", {"entities" : qUnion([Q0]), "operationType" : NewBodyOperationType.ADD, "endBound" : BoundingType.UP_TO_NEXT, "oppositeDirection" : true, "endBoundEntityFace" : qUnion([Q1]), "depth" : 25.4 * mm});
        }
    });
